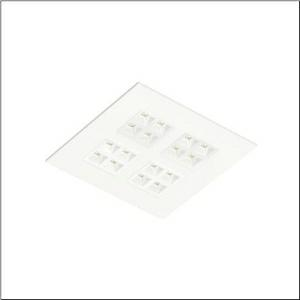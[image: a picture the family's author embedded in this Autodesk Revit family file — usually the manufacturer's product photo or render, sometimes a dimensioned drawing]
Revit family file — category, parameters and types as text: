
# Revit family: silica_31_square_51my6nds34wa
name_source: partatom
category: Lighting Fixtures
units: mm (PartAtom-declared; Revit-internal decimal feet)

## family parameters
Cut with Voids When Loaded = No
Host = Face
Light Source = No
Part Type = Normal
Room Calculation Point = No
Round Connector Dimension = Use Diameter
Shared = No

## types (1)
- --- (1 x LED, 6230 lm, 38.5 W, 3000K)
    Apparent Load = 39 VA
    CIE Flux Codes = 81 99 100 100 100
    Color Rendering = 80
    Color Temperature = 3000K
    Default Elevation = 1800 mm
    Description = Silica 31 Square, office luminaire, primary light control with lens, of PMMA, primary anti-glare with reflector, of PC, white, light emission: direct distribution, primary light characteristic: symmetric, installation type: lay-in mounting, LED, rated luminous flux: 4.540lm, luminous efficacy: 162lm/W, light colour: 830, colour temperature: 3000K, control gear: DALI 2, Multilumen, with terminal, 5-pole, mains connection: 220..240V, AC, 50/60Hz, rated input power: 28W, luminaire housing, of sheet steel, coated, traffic white (RAL 9016), module: M600, length: 595mm, width: 595mm, height: 43mm, protection rating (complete): IP20, insulation class (complete): insulation class II (safety insulation), certification: CE, impact resistance: IK03, permissible operating ambient temperature: -20..+35°C, standard: EN 50419, packaging unit: 1 piece
    Height = 0 mm  [stored 0 ft]
    Lamp = 1 x LED
    Lamp Light Flux = 6230 lm
    Lamp Power = 38.5 W
    Lamp count = 1
    Length = 595 mm
    Luminous efficacy = 162 lm/W
    Manufacturer = Siteco
    ModVariant = No
    Model = 51MY6NDS34WA
    Mounting Place = Ceiling
    Mounting Type = Recessed
    Number of Poles = 1
    OnlyDefault = Yes
    Power Factor = 1
    Product Name = Silica 31 Square
    Product group = office luminaire | ceiling recessed
    ProductGroupID = 400
    Protection Class = Protection class II
    Protection Degree = IP 20
    RLX_Detail_Level = 1
    RLX_Emergency_Light_Flux = 0 lm
    RLX_Emergency_Type = 0
    RLX_Emergency_Type_DB = No
    RlxData = <blob elided: 27921 chars, md5=74ccce83>
    Socket = socket
    Standby Power = 0 W
    System Light Flux = 6230 lm
    System Power = 39 W
    Type Comments = factory setting: luminous flux: 100 % | (OFF | OFF | OFF | OFF) | 1050 mA
    Type Image = l_1313651.jpg
    URL = http://relux.com
    VarID = @adj_042999
    Voltage = 0 V
    Weight = 0.00 kg
    Width = 595 mm

note: [stored X ft] marks values corroborated as IEEE doubles in the binary element streams (Revit-internal decimal feet)

## geometry (parser evidence)
native form markers: Blend x4, Sweep x9
no freeform markers — native parametric forms only
